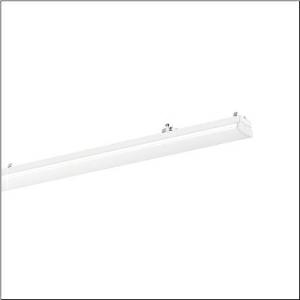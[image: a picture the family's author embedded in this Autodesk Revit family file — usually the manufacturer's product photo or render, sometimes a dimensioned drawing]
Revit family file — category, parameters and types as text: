
# Revit family: licross_21_recessed_opal_ho_52tl1dmn4e5m
name_source: partatom
category: Lighting Fixtures
units: mm (PartAtom-declared; Revit-internal decimal feet)

## family parameters
Cut with Voids When Loaded = No
Host = Face
Light Source = No
Part Type = Normal
Room Calculation Point = No
Round Connector Dimension = Use Diameter
Shared = No

## types (1)
- --- (1 x LED, 14660 lm, 83.1 W, 4000K)
    Apparent Load = 83 VA
    CIE Flux Codes = 44 73 91 87 100
    Color Rendering = 80
    Color Temperature = 4000K
    Default Elevation = 1800 mm
    Description = Licross 21 recessed opal HO, luminaire insert, of sheet steel, galvanised, coil coated, white, length: 1.500mm, width: 66mm, height: 67mm, LED rated luminous flux: 14.660lm, light colour: 840, SDCM (Standard Deviation of Colour Matching)MacAdam ≤ 3 SDCM (initial), control gear: ON/OFF Multilumen, with plug, 3-pole, with phase selection, mains connection: 220..240V, AC, 50/60Hz, rated input power: 83W, internal wiring halogen-free, primary optical cover: cover, of PMMA, light emission: direct with ceiling illumination distribution, primary light characteristic: symmetric, protection rating (complete): IP40, insulation class (complete): insulation class I (protective earthing), certification: CE, ENEC, VDE, UKCA, protection symbol: D if used in an environment without relevant dust loads with corresponding accessories, impact resistance: IK06, permissible ambient temperature for indoor applications: -35..+30°C, corresponds to IFS (International Featured Standards) requirements for safety and quality in the food industry, reducing of maximum allowable ambient temperature of 5°C with ceiling mounting, LABS conformity tested according to VDMA 24364:2018-05, The light source and the operating device comply with the requirements of the Ecodesign Regulation (EU) 2019/2020 and are replaceable in accordance with this regulation, packaging unit: 1 piece
    Height = 83 mm
    Lamp = 1 x LED
    Lamp Light Flux = 14660 lm
    Lamp Power = 83.1 W
    Lamp count = 1
    Length = 1500 mm
    Luminous efficacy = 176 lm/W
    Manufacturer = Siteco
    ModVariant = No
    Model = 52TL1DMN4E5M
    Mounting Place = Ceiling
    Mounting Type = Pendant
    Number of Poles = 1
    OnlyDefault = Yes
    Power Factor = 1
    Product Name = Licross 21 recessed opal HO
    Product group = luminaire insert | ceiling pendant
    ProductGroupID = 901
    Protection Class = Protection class I
    Protection Degree = IP 40
    RLX_Detail_Level = 1
    RLX_Emergency_Light_Flux = 0 lm
    RLX_Emergency_Type = 0
    RLX_Emergency_Type_DB = No
    RlxData = <blob elided: 25053 chars, md5=b05a1541>
    Socket = socket
    Standby Power = 0 W
    System Light Flux = 14660 lm
    System Power = 83 W
    Type Comments = factory setting: luminous flux: 100 % | (A | C | E) | 195 mA
    Type Image = l_1313666.jpg
    URL = http://relux.com
    VarID = @adj_072325
    Voltage = 0 V
    Weight = 0.00 kg
    Width = 76 mm

## geometry (parser evidence)
native form markers: Blend x4, Sweep x13
no freeform markers — native parametric forms only
